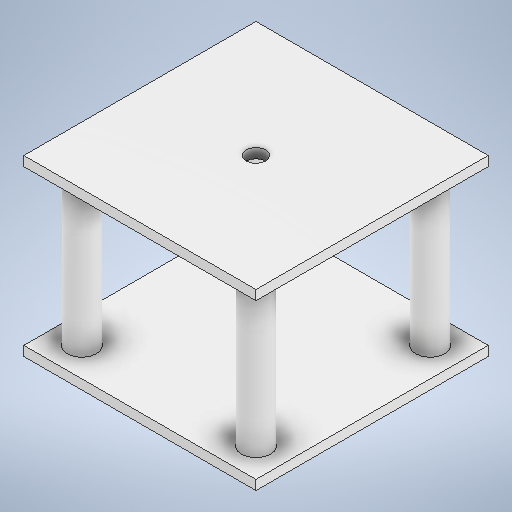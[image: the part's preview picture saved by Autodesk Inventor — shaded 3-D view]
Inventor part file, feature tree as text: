
AUTODESK INVENTOR PART (.ipt)
format: ipt  version: 2025.3 (Build 293356000, 356)  size: 229,888 bytes
history: native  units: mm
features: extrude x4, sketch x4, other x1
ambient origin geometry x8: Origin, YZ Plane, XZ Plane, XY Plane, X Axis, Y Axis, Z Axis, Center Point
bodies: Body1 (feature_tree)
feature tree (9):
  other  "Sólido1"
  extrude  "Extrusión1"  Depth=120.0mm
  extrude  "Extrusión2"  Depth=90.0mm
  extrude  "Extrusión3"  Depth=90.0mm
  extrude  "Extrusión4"  Depth=10.0mm
  sketch  "Boceto1"  dims[d0=120.0mm d1=120.0mm]
  sketch  "Boceto2"  dims[d2=5.0mm d3=0.0mm d4=90.0mm]
  sketch  "Boceto3"  dims[d5=90.0mm d6=15.0mm]
  sketch  "Boceto4"  dims[d7=15.0mm d8=15.0mm d9=15.0mm d10=80.0mm d11=0.0mm d12=120.0mm d13=120.0mm d14=5.0mm d15=0.0mm d16=10.0mm d17=10.0mm d18=0.0mm d19=0.5mm d20=0.872665mm]
